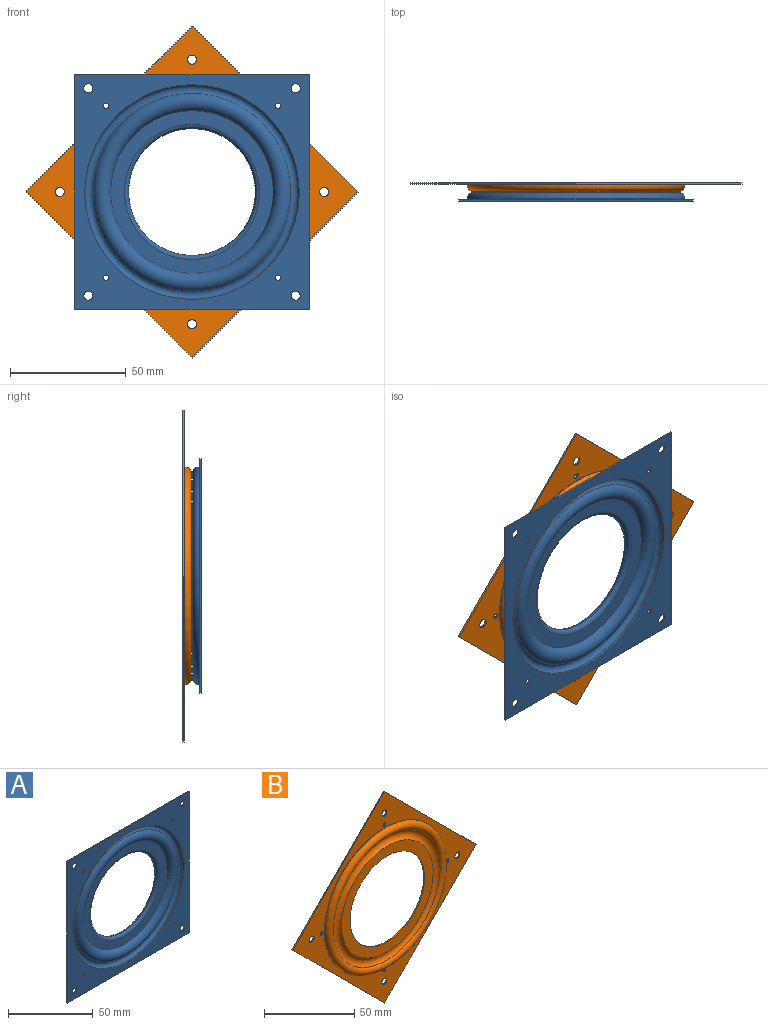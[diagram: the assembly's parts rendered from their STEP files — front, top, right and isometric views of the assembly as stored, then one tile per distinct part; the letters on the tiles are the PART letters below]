
ASSEMBLY  parts=2 mates=1
PART A: 28 faces, bbox 102.1x6.6x102.1 mm
  f0: torus R=29.21mm, axis (0,1,0), area 492.7mm2, adj f11,f12
  f1: plane 101.6x101.6mm, normal (0,-1,0), area 3483.6mm2, adj f15,f16,f17,f18,f19,f20,f21,f22
  f2: plane 101.6x101.6mm, normal (0,1,0), area 3267mm2, adj f3,f16,f17,f18,f19,f20,f21,f22
  f3: cylinder r=47.16mm len=94.33mm, axis (0,1,0), area 82.8mm2, adj f2,f4
  f4: torus R=44.4mm, axis (0,1,0), area 2045.9mm2, adj f3,f5
  f5: torus R=39.12mm, axis (0,1,0), area 2043.3mm2, adj f4,f6
  f6: plane 71.6x71.6mm, normal (0,1,0), area 1346mm2, adj f5,f7
  f7: torus R=29.21mm, axis (0,1,0), area 586.8mm2, adj f6,f8
  f8: plane 64.39x64.39mm, normal (0,-1,0), area 575.9mm2, adj f7,f9
  f9: cylinder r=32.2mm len=64.39mm, axis (0,1,0), area 149mm2, adj f8,f10
  f10: plane 64.39x64.39mm, normal (0,1,0), area 575.9mm2, adj f9,f11
  f11: torus R=29.21mm, axis (0,1,0), area 492.7mm2, adj f0,f10
  f12: plane 70.36x70.36mm, normal (0,-1,0), area 1207.9mm2, adj f0,f13
  f13: torus R=39.12mm, axis (0,1,0), area 2336.6mm2, adj f12,f14
  f14: torus R=44.4mm, axis (0,1,0), area 1496.9mm2, adj f13,f15
  f15: cylinder r=46.43mm len=92.85mm, axis (0,1,0), area 296.4mm2, adj f1,f14
  f16: plane 101.6x0.74mm, normal (0,0,-1), area 74.8mm2, adj f1,f2,f17,f19
  f17: plane 101.6x0.74mm, normal (-1,0,0), area 74.8mm2, adj f1,f2,f16,f18
  f18: plane 101.6x0.74mm, normal (0,0,1), area 74.8mm2, adj f1,f2,f17,f19
  f19: plane 101.6x0.74mm, normal (1,0,0), area 74.8mm2, adj f1,f2,f16,f18
  f20: cylinder r=1.98mm len=3.97mm, axis (0,1,0), area 9.2mm2, adj f1,f2
  f21: cylinder r=1.98mm len=3.97mm, axis (0,1,0), area 9.2mm2, adj f1,f2
  f22: cylinder r=1.98mm len=3.97mm, axis (0,1,0), area 9.2mm2, adj f1,f2
  f23: cylinder r=1.98mm len=3.97mm, axis (0,1,0), area 9.2mm2, adj f1,f2
  f24: cylinder r=1.19mm len=2.38mm, axis (0,1,0), area 5.5mm2, adj f1,f2
  f25: cylinder r=1.19mm len=2.38mm, axis (0,1,0), area 5.5mm2, adj f1,f2
  f26: cylinder r=1.19mm len=2.38mm, axis (0,1,0), area 5.5mm2, adj f1,f2
  f27: cylinder r=1.19mm len=2.38mm, axis (0,1,0), area 5.5mm2, adj f1,f2
PART B: 23 faces, bbox 143.7x5x143.7 mm
  f0: plane 143.68x143.68mm, normal (0,-1,0), area 3267mm2, adj f10,f11,f12,f13,f14,f15,f16,f17
  f1: plane 143.68x143.68mm, normal (0,1,0), area 3483.6mm2, adj f2,f11,f12,f13,f14,f15,f16,f17
  f2: cylinder r=46.43mm len=92.85mm, axis (0,1,0), area 296.4mm2, adj f1,f3
  f3: torus R=44.4mm, axis (0,1,0), area 1496.9mm2, adj f2,f4
  f4: torus R=39.12mm, axis (0,1,0), area 2149.8mm2, adj f3,f5
  f5: plane 70.95x70.95mm, normal (0,1,0), area 1272.9mm2, adj f4,f6
  f6: cylinder r=29.21mm len=58.42mm, axis (0,1,0), area 135.2mm2, adj f5,f7
  f7: plane 71.93x71.93mm, normal (0,-1,0), area 1382.9mm2, adj f6,f8
  f8: torus R=39.12mm, axis (0,1,0), area 1861.6mm2, adj f7,f9
  f9: torus R=44.4mm, axis (0,1,0), area 2045.9mm2, adj f8,f10
  f10: cylinder r=47.16mm len=94.33mm, axis (0,1,0), area 82.8mm2, adj f0,f9
  f11: plane 71.84x71.84mm, normal (-0.71,0,-0.71), area 74.8mm2, adj f0,f1,f12,f14
  f12: plane 71.84x71.84mm, normal (-0.71,0,0.71), area 74.8mm2, adj f0,f1,f11,f13
  f13: plane 71.84x71.84mm, normal (0.71,0,0.71), area 74.8mm2, adj f0,f1,f12,f14
  f14: plane 71.84x71.84mm, normal (0.71,0,-0.71), area 74.8mm2, adj f0,f1,f11,f13
  f15: cylinder r=1.98mm len=3.97mm, axis (0,1,0), area 9.2mm2, adj f0,f1
  f16: cylinder r=1.98mm len=3.97mm, axis (0,1,0), area 9.2mm2, adj f0,f1
  f17: cylinder r=1.98mm len=3.97mm, axis (0,1,0), area 9.2mm2, adj f0,f1
  f18: cylinder r=1.98mm len=3.97mm, axis (0,1,0), area 9.2mm2, adj f0,f1
  f19: cylinder r=1.19mm len=2.38mm, axis (0,1,0), area 5.5mm2, adj f0,f1
  f20: cylinder r=1.19mm len=2.38mm, axis (0,1,0), area 5.5mm2, adj f0,f1
  f21: cylinder r=1.19mm len=2.38mm, axis (0,1,0), area 5.5mm2, adj f0,f1
  f22: cylinder r=1.19mm len=2.38mm, axis (0,1,0), area 5.5mm2, adj f0,f1
PLACE A at identity
PLACE B at identity fixed
MATE cylindrical A.f0 <-> B.f2  axis (0,-1,0) through (0,1.04,0)mm
